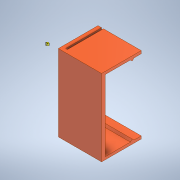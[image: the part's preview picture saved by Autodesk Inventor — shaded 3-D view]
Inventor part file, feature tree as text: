
AUTODESK INVENTOR PART (.ipt)
format: ipt  version: 2021.2 (Build 252289000, 289)  size: 471,040 bytes
history: native  units: in
note: dims shown in document units (in); Inventor stores cm internally (conversion verified against a paired STEP export)
features: extrude x7, sketch x7, mirror x1
ambient origin geometry x8: Origin, YZ Plane, XZ Plane, XY Plane, X Axis, Y Axis, Z Axis, Center Point
bodies: Solid1 (feature_tree)
feature tree (15):
  extrude  "Extrusion1"  Depth=1.2in
  extrude  "Extrusion7"  TaperAngle=0.0deg  [1 undecoded]
  extrude  "Extrusion8"  Depth=0.075in
  extrude  "Extrusion9"  Depth=0.3875in
  extrude  "Extrusion10"  Depth=0.1in
  extrude  "Extrusion11"  Depth=0.24in TaperAngle=0.0deg
  extrude  "Extrusion12"  TaperAngle=135.0deg  [1 undecoded]
  mirror  "Mirror1"
  sketch  "Sketch1"  dims[d0=2.125in d1=1.2in]
  sketch  "Sketch8"  dims[d2=0.1in d3=0.0in]
  sketch  "Sketch10"  dims[d32=0.075in d33=0.075in]
  sketch  "Sketch11"  dims[d34=0.1in d35=0.3875in]
  sketch  "Sketch12"  dims[d36=0.3875in d37=0.1in]
  sketch  "Sketch13"  dims[d38=1.0in d39=0.0in d40=0.24in d41=0.0in]
  sketch  "Sketch14"  dims[d42=90.0deg d43=135.0deg d44=0.05in d45=0.25in d46=0.24in d47=0.0in d48=0.05in d49=0.0in d50=0.0in d51=0.55in d52=0.05in d53=0.0in d54=1.2in d55=0.25in d56=0.0625in d57=0.0in]
note: 2 required parameter values undecoded (feature->parameter linkage not recoverable at this tier; creation-order binding heuristic only, values carry confidence <= 0.55)
